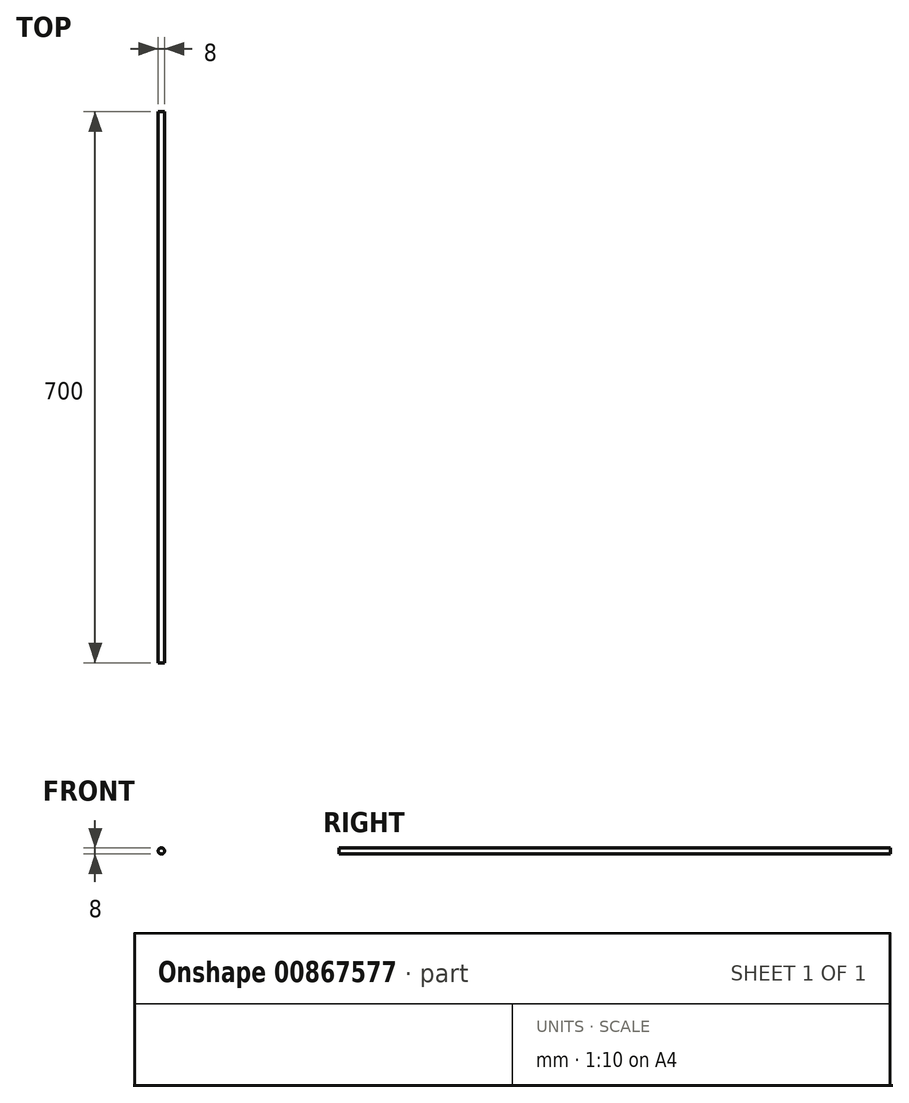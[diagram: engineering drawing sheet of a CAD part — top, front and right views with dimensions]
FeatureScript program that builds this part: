
annotation { "Feature Type Name" : "Feature", "Feature Type Description" : "" }
export const myFeature = defineFeature(function(context is Context, id is Id, definition is map)
    precondition{}
    {
        {
            var Q0;
            Q0=qCreatedBy(makeId("Front.planeOp"),FACE);
            var sketch = newSketch(context, id + "F0", { "sketchPlane" : qUnion([Q0])});
            skCircle(sketch, "E0", {"center": v(0, 0) * mm, "radius": 4 * mm});
            skSolve(sketch);
        }
        {
            var Q0;
            Q0=makeQuery(id+"F0.imprint","IMPRINT",FACE,{"disambiguationData":[TD([[makeQuery(id+"F0.imprint","IMPRINT",EDGE,{"derivedFrom":sQuery(id+"F0.wireOp",EDGE,"E0")}),1.0]])]});
            extrude(context, id + "F1", {"entities" : qUnion([Q0]), "depth" : 700 * mm, "offsetDistance" : 25 * mm});
        }
    });
